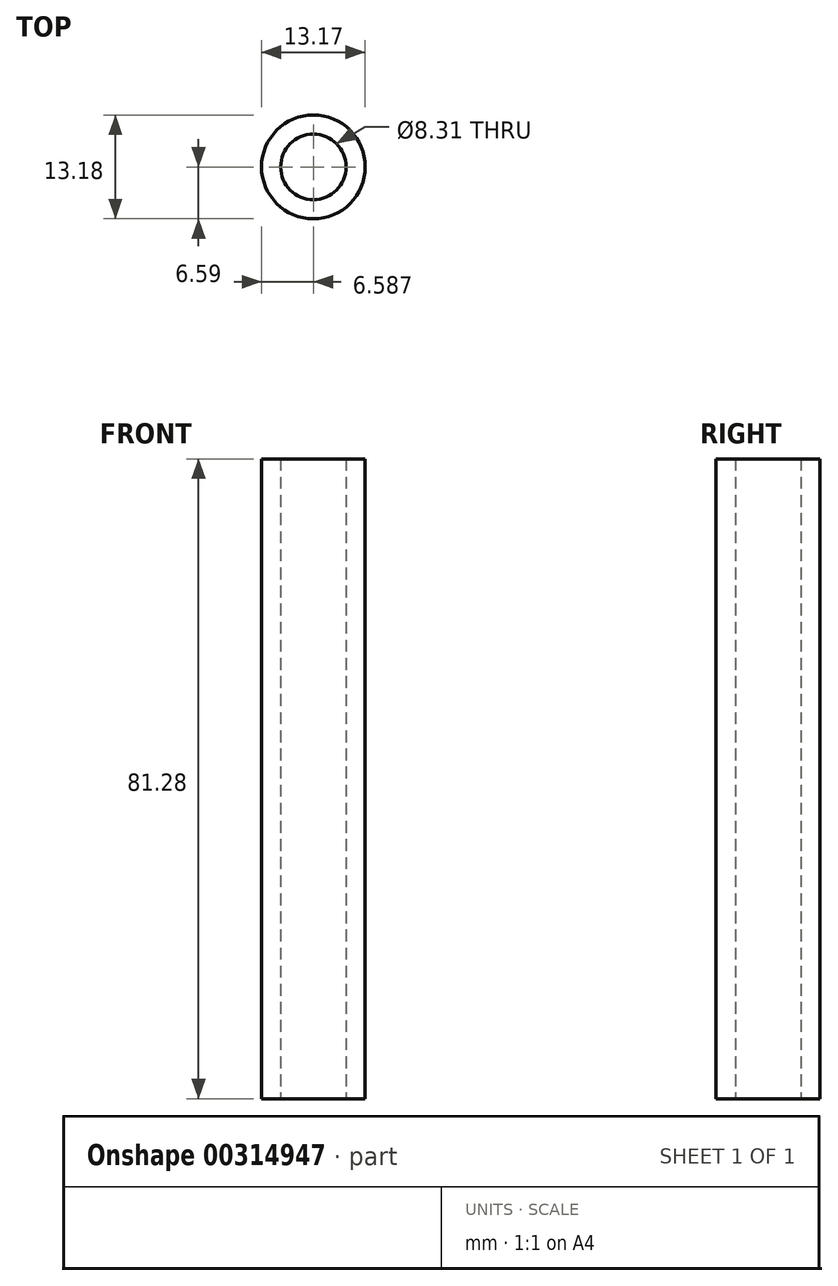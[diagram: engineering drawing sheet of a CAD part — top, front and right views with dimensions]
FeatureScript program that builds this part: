
annotation { "Feature Type Name" : "Feature", "Feature Type Description" : "" }
export const myFeature = defineFeature(function(context is Context, id is Id, definition is map)
    precondition{}
    {
        {
            var Q0;
            Q0=qCreatedBy(makeId("Top.planeOp"),FACE);
            var sketch = newSketch(context, id + "F0", { "sketchPlane" : qUnion([Q0])});
            skCircle(sketch, "E0", {"center": v(-38.88, 0) * mm, "radius": 4.15 * mm});
            skCircle(sketch, "E1", {"center": v(-38.88, 0) * mm, "radius": 6.59 * mm});
            skSolve(sketch);
        }
        {
            var Q0;
            Q0 = qSketchRegion(id + "F0", true);
            extrude(context, id + "F1", {"entities" : qUnion([Q0]), "depth" : 81.28 * mm});
        }
    });
